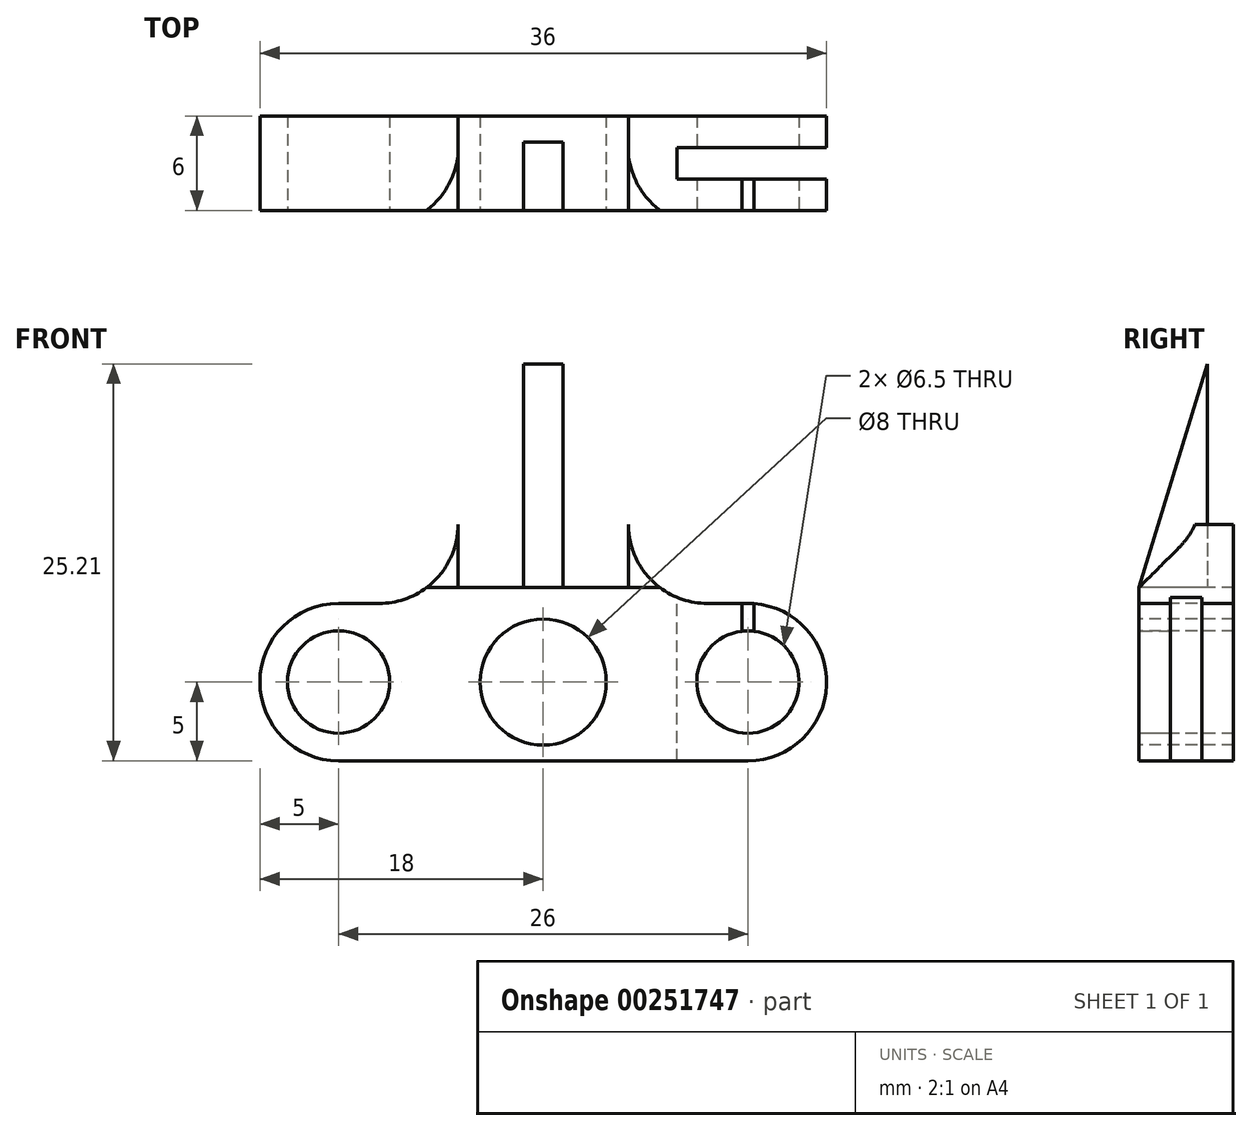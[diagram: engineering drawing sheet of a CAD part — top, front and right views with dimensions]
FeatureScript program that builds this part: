
annotation { "Feature Type Name" : "Feature", "Feature Type Description" : "" }
export const myFeature = defineFeature(function(context is Context, id is Id, definition is map)
    precondition{}
    {
        {
            var Q0;
            Q0=qCreatedBy(makeId("Front.planeOp"),FACE);
            var sketch = newSketch(context, id + "F0", { "sketchPlane" : qUnion([Q0])});
            skLineSegment(sketch, "E0.bottom", {"start": v(13, -5) * mm, "end": v(-13, -5) * mm});
            skLineSegment(sketch, "E0.top", {"start": v(13, 5) * mm, "end": v(10.41, 5) * mm});
            skPoint(sketch, "E0.middle", {"position": v(0, 0) * mm});
            skLineSegment(sketch, "E1", {"start": v(-5.41, 6) * mm, "end": v(5.41, 6) * mm});
            skLineSegment(sketch, "E2.bottom", {"start": v(5.41, 6) * mm, "end": v(-5.41, 6) * mm});
            skLineSegment(sketch, "E2.left", {"start": v(5.41, 6) * mm, "end": v(5.41, 23.5) * mm});
            skLineSegment(sketch, "E2.right", {"start": v(-5.41, 6) * mm, "end": v(-5.41, 23.5) * mm});
            skPoint(sketch, "E2.middle", {"position": v(0, 14.75) * mm});
            skArc(sketch, "E3", {"start": v(-13, 5) * mm, "mid": v(-18, 0) * mm, "end": v(-13, -5) * mm});
            skArc(sketch, "E4", {"start": v(13, -5) * mm, "mid": v(18, 0) * mm, "end": v(13, 5) * mm});
            skCircle(sketch, "E5", {"center": v(-13, 0) * mm, "radius": 3.25 * mm});
            skCircle(sketch, "E6", {"center": v(13, 0) * mm, "radius": 3.25 * mm});
            skCircle(sketch, "E7", {"center": v(0, 0) * mm, "radius": 4 * mm});
            skLineSegment(sketch, "E8.trimOffspring", {"start": v(-10.41, 5) * mm, "end": v(-13, 5) * mm});
            skPoint(sketch, "E9.end.orphan", {"position": v(-8.5, 6) * mm});
            skLineSegment(sketch, "E10", {"start": v(-5.41, 10) * mm, "end": v(-5.41, 6) * mm});
            skLineSegment(sketch, "E11", {"start": v(5.41, 10) * mm, "end": v(5.41, 6) * mm});
            skArc(sketch, "E12", {"start": v(5.41, 23.5) * mm, "mid": v(0, 28.91) * mm, "end": v(-5.41, 23.5) * mm});
            skCircle(sketch, "E13", {"center": v(0, 23.5) * mm, "radius": 3 * mm});
            skPoint(sketch, "E14.visualSharp", {"position": v(-5.41, 0) * mm});
            skPoint(sketch, "E15.visualSharp", {"position": v(5.41, 0) * mm});
            skArc(sketch, "E16", {"start": v(-10.41, 5) * mm, "mid": v(-6.88, 6.46) * mm, "end": v(-5.41, 10) * mm});
            skArc(sketch, "E17.MirrorCS", {"start": v(10.41, 5) * mm, "mid": v(6.88, 6.46) * mm, "end": v(5.41, 10) * mm});
            skSolve(sketch);
        }
        {
            var Q0;
            Q0=makeQuery(id+"F0.imprint","IMPRINT",FACE,{"disambiguationData":[TD([[makeQuery(id+"F0.imprint","IMPRINT",EDGE,{"derivedFrom":sQuery(id+"F0.wireOp",EDGE,"E0.bottom")}),-1.0]])]});
            var Q1;
            Q1=makeQuery(id+"F0.imprint","IMPRINT",FACE,{"disambiguationData":[TD([[makeQuery(id+"F0.imprint","IMPRINT",EDGE,{"derivedFrom":sQuery(id+"F0.wireOp",EDGE,"E2.bottom")}),-1.0]])]});
            extrude(context, id + "F1", {"entities" : qUnion([Q0, Q1]), "endBound" : BoundingType.SYMMETRIC, "oppositeDirection" : true, "depth" : 6 * mm});
        }
        {
            var Q0;
            Q0=qCreatedBy(makeId("Right.planeOp"),FACE);
            var sketch = newSketch(context, id + "F2", { "sketchPlane" : qUnion([Q0])});
            skLineSegment(sketch, "E18", {"start": v(-3, 28.91) * mm, "end": v(1, 28.91) * mm});
            skLineSegment(sketch, "E19", {"start": v(1, 28.91) * mm, "end": v(1, 12.07) * mm});
            skPoint(sketch, "E20.0", {"position": v(0, 6) * mm});
            skLineSegment(sketch, "E21.0", {"start": v(-3, 6) * mm, "end": v(-3, 10) * mm});
            skPoint(sketch, "E22.orphan", {"position": v(-3, 5) * mm});
            skLineSegment(sketch, "E23.0", {"start": v(-3, 23.5) * mm, "end": v(-3, 28.91) * mm});
            skLineSegment(sketch, "E24.0", {"start": v(-3, 10) * mm, "end": v(-3, 23.5) * mm});
            skLineSegment(sketch, "E25.0.0", {"start": v(-3, 10) * mm, "end": v(-3, 6) * mm});
            skPoint(sketch, "E25.0.2.start.orphan", {"position": v(3, 5) * mm});
            skPoint(sketch, "E26.orphan", {"position": v(3, 10) * mm});
            skLineSegment(sketch, "E27", {"start": v(-3, 6) * mm, "end": v(-0.46, 8.54) * mm});
            skArc(sketch, "E28", {"start": v(-0.46, 8.54) * mm, "mid": v(0.62, 10.16) * mm, "end": v(1, 12.07) * mm});
            skSolve(sketch);
        }
        {
            var Q0;
            Q0 = qSketchRegion(id + "F2", true);
            extrude(context, id + "F3", {"entities" : qUnion([Q0]), "operationType" : NewBodyOperationType.REMOVE, "endBound" : BoundingType.SYMMETRIC, "oppositeDirection" : true, "depth" : 25 * mm});
        }
        {
            var Q0;
            Q0=qCreatedBy(makeId("Right.planeOp"),FACE);
            var sketch = newSketch(context, id + "F4", { "sketchPlane" : qUnion([Q0])});
            skPoint(sketch, "E29.0", {"position": v(-3, 6) * mm});
            skLineSegment(sketch, "E30", {"start": v(-3, 6) * mm, "end": v(1.35, 20.21) * mm});
            skLineSegment(sketch, "E31", {"start": v(1.35, 6) * mm, "end": v(-3, 6) * mm});
            skLineSegment(sketch, "E32.0", {"start": v(1, 23.5) * mm, "end": v(1, 12.07) * mm});
            skLineSegment(sketch, "E33", {"start": v(1.35, 20.21) * mm, "end": v(1.35, 6) * mm});
            skSolve(sketch);
        }
        {
            var Q0;
            Q0 = qSketchRegion(id + "F4", true);
            extrude(context, id + "F5", {"entities" : qUnion([Q0]), "operationType" : NewBodyOperationType.ADD, "endBound" : BoundingType.SYMMETRIC, "depth" : 2.5 * mm});
        }
        {
            var Q0;
            Q0=qCreatedBy(makeId("Top.planeOp"),FACE);
            var sketch = newSketch(context, id + "F6", { "sketchPlane" : qUnion([Q0])});
            skLineSegment(sketch, "E34", {"start": v(18, 1) * mm, "end": v(18, -1) * mm});
            skLineSegment(sketch, "E35.bottom", {"start": v(18, -1) * mm, "end": v(8.5, -1) * mm});
            skLineSegment(sketch, "E35.top", {"start": v(18, 1) * mm, "end": v(8.5, 1) * mm});
            skLineSegment(sketch, "E35.left", {"start": v(18, -1) * mm, "end": v(18, 1) * mm});
            skLineSegment(sketch, "E35.right", {"start": v(8.5, -1) * mm, "end": v(8.5, 1) * mm});
            skPoint(sketch, "E35.middle", {"position": v(13.25, 0) * mm});
            skSolve(sketch);
        }
        {
            var Q0;
            Q0 = qSketchRegion(id + "F6", true);
            extrude(context, id + "F7", {"entities" : qUnion([Q0]), "operationType" : NewBodyOperationType.REMOVE, "endBound" : BoundingType.SYMMETRIC, "oppositeDirection" : true, "depth" : 25 * mm});
        }
        {
            var Q0;
            Q0=makeQuery(id+"F1.opExtrude","CAP_FACE",FACE,{"disambiguationData":[OSD([sQuery(id+"F0.wireOp",EDGE,"E0.bottom"),sQuery(id+"F0.wireOp",EDGE,"E0.top"),sQuery(id+"F0.wireOp",EDGE,"E2.left"),sQuery(id+"F0.wireOp",EDGE,"E2.right"),sQuery(id+"F0.wireOp",EDGE,"E3"),sQuery(id+"F0.wireOp",EDGE,"E4"),sQuery(id+"F0.wireOp",EDGE,"E5"),sQuery(id+"F0.wireOp",EDGE,"E6"),sQuery(id+"F0.wireOp",EDGE,"E7"),sQuery(id+"F0.wireOp",EDGE,"E8.trimOffspring"),sQuery(id+"F0.wireOp",EDGE,"E12"),sQuery(id+"F0.wireOp",EDGE,"E13"),sQuery(id+"F0.wireOp",EDGE,"E16"),sQuery(id+"F0.wireOp",EDGE,"E17.MirrorCS")])],"isStart":true});
            var sketch = newSketch(context, id + "F8", { "sketchPlane" : qUnion([Q0])});
            skLineSegment(sketch, "E36.bottom", {"start": v(13.38, 3) * mm, "end": v(12.62, 3) * mm});
            skLineSegment(sketch, "E36.top", {"start": v(13.38, 7) * mm, "end": v(12.62, 7) * mm});
            skLineSegment(sketch, "E36.left", {"start": v(13.38, 3) * mm, "end": v(13.38, 7) * mm});
            skLineSegment(sketch, "E36.right", {"start": v(12.62, 3) * mm, "end": v(12.62, 7) * mm});
            skPoint(sketch, "E36.middle", {"position": v(13, 5) * mm});
            skSolve(sketch);
        }
        {
            var Q0;
            Q0 = qSketchRegion(id + "F8", true);
            extrude(context, id + "F9", {"entities" : qUnion([Q0]), "operationType" : NewBodyOperationType.REMOVE, "oppositeDirection" : true, "depth" : 2 * mm});
        }
    });
